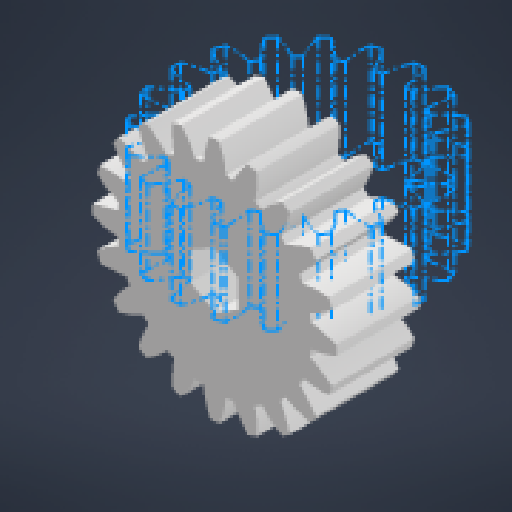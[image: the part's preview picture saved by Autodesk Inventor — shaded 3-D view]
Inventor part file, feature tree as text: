
AUTODESK INVENTOR PART (.ipt)
format: ipt  version: 2024 (Build 280153000, 153)  size: 230,400 bytes
history: native  units: mm
features: other x4, extrude x1, sketch x1
ambient origin geometry x8: Origin, YZ Plane, XZ Plane, XY Plane, X Axis, Y Axis, Z Axis, Center Point
bodies: Body1 (feature_tree)
feature tree (6):
  other  "{BB8FE430-83BF-418D-8DF9-9B323D3DB9B9}"
  other  "솔리드1"
  extrude  "돌출1"  Depth=44.31mm
  other  "스퍼 기어 톱니1"
  sketch  "스케치1"
  other  "스퍼 기어1"
